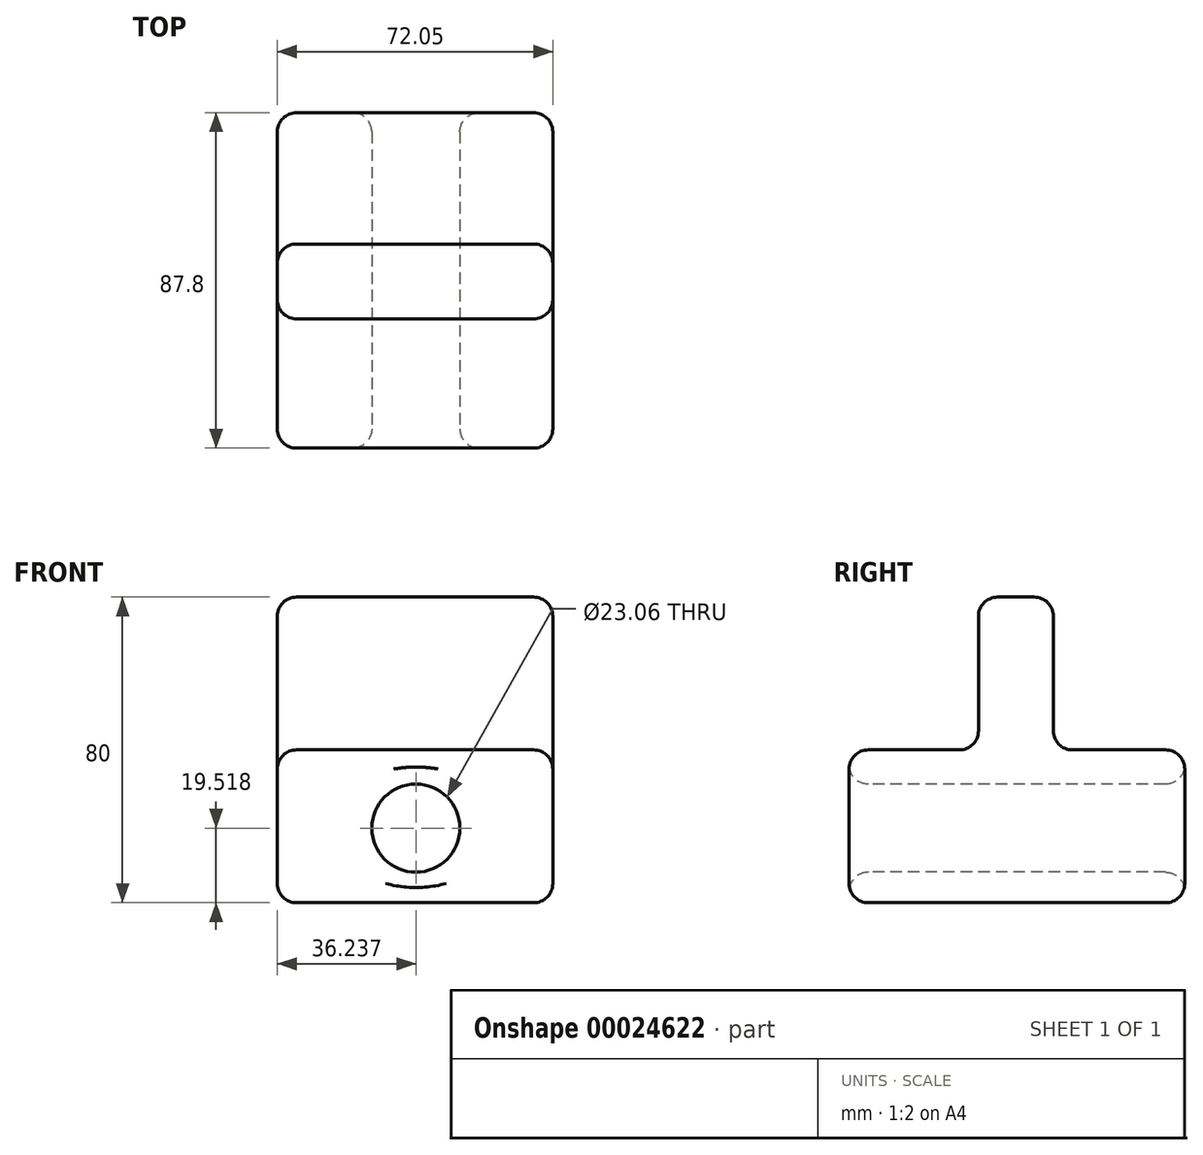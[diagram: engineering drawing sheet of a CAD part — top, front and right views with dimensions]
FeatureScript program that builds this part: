
annotation { "Feature Type Name" : "Feature", "Feature Type Description" : "" }
export const myFeature = defineFeature(function(context is Context, id is Id, definition is map)
    precondition{}
    {
        {
            var Q0;
            Q0=qCreatedBy(makeId("Top.planeOp"),FACE);
            var sketch = newSketch(context, id + "F0", { "sketchPlane" : qUnion([Q0])});
            skLineSegment(sketch, "E0.bottom", {"start": v(-59.89, -44.54) * mm, "end": v(12.16, -44.54) * mm});
            skLineSegment(sketch, "E0.top", {"start": v(-59.89, 43.26) * mm, "end": v(12.16, 43.26) * mm});
            skLineSegment(sketch, "E0.left", {"start": v(-59.89, -44.54) * mm, "end": v(-59.89, 43.26) * mm});
            skLineSegment(sketch, "E0.right", {"start": v(12.16, -44.54) * mm, "end": v(12.16, 43.26) * mm});
            skSolve(sketch);
        }
        {
            var Q0;
            Q0=makeQuery(id+"F0.imprint","IMPRINT",FACE,{"disambiguationData":[TD([[makeQuery(id+"F0.imprint","IMPRINT",EDGE,{"derivedFrom":sQuery(id+"F0.wireOp",EDGE,"E0.bottom")}),1.0]])]});
            extrude(context, id + "F1", {"entities" : qUnion([Q0]), "depth" : 40 * mm});
        }
        {
            var Q0;
            Q0=makeQuery(id+"F1.opExtrude","SWEPT_FACE",FACE,{"disambiguationData":[OSD([sQuery(id+"F0.wireOp",EDGE,"E0.bottom")])]});
            var sketch = newSketch(context, id + "F2", { "sketchPlane" : qUnion([Q0])});
            skCircle(sketch, "E1", {"center": v(-23.65, 19.52) * mm, "radius": 11.53 * mm});
            skSolve(sketch);
        }
        {
            var Q0;
            Q0=makeQuery(id+"F2.imprint","IMPRINT",FACE,{"disambiguationData":[TD([[makeQuery(id+"F2.imprint","IMPRINT",EDGE,{"derivedFrom":sQuery(id+"F2.wireOp",EDGE,"E1")}),1.0]])]});
            extrude(context, id + "F3", {"entities" : qUnion([Q0]), "operationType" : NewBodyOperationType.REMOVE, "endBound" : BoundingType.THROUGH_ALL, "oppositeDirection" : true, "depth" : 25 * mm});
        }
        {
            var Q0;
            Q0=makeQuery(id+"F1.opExtrude","CAP_FACE",FACE,{"disambiguationData":[OSD([sQuery(id+"F0.wireOp",EDGE,"E0.bottom"),sQuery(id+"F0.wireOp",EDGE,"E0.top"),sQuery(id+"F0.wireOp",EDGE,"E0.left"),sQuery(id+"F0.wireOp",EDGE,"E0.right")])],"isStart":false});
            var sketch = newSketch(context, id + "F4", { "sketchPlane" : qUnion([Q0])});
            skLineSegment(sketch, "E2.bottom", {"start": v(-59.89, -10.7) * mm, "end": v(12.16, -10.7) * mm});
            skLineSegment(sketch, "E2.top", {"start": v(-59.89, 8.88) * mm, "end": v(12.16, 8.88) * mm});
            skLineSegment(sketch, "E2.left", {"start": v(-59.89, -10.7) * mm, "end": v(-59.89, 8.88) * mm});
            skLineSegment(sketch, "E2.right", {"start": v(12.16, -10.7) * mm, "end": v(12.16, 8.88) * mm});
            skSolve(sketch);
        }
        {
            var Q0;
            Q0=makeQuery(id+"F4.imprint","IMPRINT",FACE,{"disambiguationData":[TD([[makeQuery(id+"F4.imprint","IMPRINT",EDGE,{"derivedFrom":sQuery(id+"F4.wireOp",EDGE,"E2.bottom")}),1.0]])]});
            extrude(context, id + "F5", {"entities" : qUnion([Q0]), "operationType" : NewBodyOperationType.ADD, "depth" : 40 * mm});
        }
        {
            var Q0;
            Q0=makeQuery(id+"F5.opExtrude","SWEPT_FACE",FACE,{"disambiguationData":[OSD([sQuery(id+"F4.wireOp",EDGE,"E2.bottom")])]});
            var Q1;
            {var subQ0=sQuery(id+"F0.wireOp",EDGE,"E0.bottom");var subQ1=sQuery(id+"F0.wireOp",EDGE,"E0.left");var subQ2=sQuery(id+"F0.wireOp",EDGE,"E0.right");Q1=makeQuery(id+"F5.boolean.opBoolean","SPLIT",FACE,{"disambiguationData":[TD([makeQuery(id+"F1.opExtrude","SWEPT_FACE",FACE,{"disambiguationData":[OSD([subQ0])]})])],"derivedFrom":makeQuery(id+"F1.opExtrude","CAP_FACE",FACE,{"disambiguationData":[OSD([subQ0,sQuery(id+"F0.wireOp",EDGE,"E0.top"),subQ1,subQ2])],"isStart":false})});}
            var Q2;
            Q2=makeQuery(id+"F5.boolean.opBoolean","MERGE",FACE,{"derivedFrom":[makeQuery(id+"F1.opExtrude","SWEPT_FACE",FACE,{"disambiguationData":[OSD([sQuery(id+"F0.wireOp",EDGE,"E0.right")])]}),makeQuery(id+"F5.opExtrude","SWEPT_FACE",FACE,{"disambiguationData":[OSD([sQuery(id+"F4.wireOp",EDGE,"E2.right")])]})]});
            var Q3;
            Q3=makeQuery(id+"F1.opExtrude","SWEPT_FACE",FACE,{"disambiguationData":[OSD([sQuery(id+"F0.wireOp",EDGE,"E0.bottom")])]});
            var Q4;
            Q4=makeQuery(id+"F3.boolean.opBoolean","COPY",FACE,{"derivedFrom":makeQuery(id+"F3.opExtrude","SWEPT_FACE",FACE,{"disambiguationData":[OSD([sQuery(id+"F2.wireOp",EDGE,"E1")])]})});
            var Q5;
            Q5=makeQuery(id+"F5.opExtrude","SWEPT_FACE",FACE,{"disambiguationData":[OSD([sQuery(id+"F4.wireOp",EDGE,"E2.top")])]});
            var Q6;
            Q6=makeQuery(id+"F1.opExtrude","SWEPT_FACE",FACE,{"disambiguationData":[OSD([sQuery(id+"F0.wireOp",EDGE,"E0.top")])]});
            var Q7;
            Q7=makeQuery(id+"F1.opExtrude","CAP_FACE",FACE,{"disambiguationData":[OSD([sQuery(id+"F0.wireOp",EDGE,"E0.bottom"),sQuery(id+"F0.wireOp",EDGE,"E0.top"),sQuery(id+"F0.wireOp",EDGE,"E0.left"),sQuery(id+"F0.wireOp",EDGE,"E0.right")])],"isStart":true});
            var Q8;
            Q8=makeQuery(id+"F5.boolean.opBoolean","MERGE",FACE,{"derivedFrom":[makeQuery(id+"F1.opExtrude","SWEPT_FACE",FACE,{"disambiguationData":[OSD([sQuery(id+"F0.wireOp",EDGE,"E0.left")])]}),makeQuery(id+"F5.opExtrude","SWEPT_FACE",FACE,{"disambiguationData":[OSD([sQuery(id+"F4.wireOp",EDGE,"E2.left")])]})]});
            fillet(context, id + "F6", {"entities" : qUnion([Q0, Q1, Q2, Q3, Q4, Q5, Q6, Q7, Q8]), "radius" : 5 * mm, "tangentPropagation" : true, "allowEdgeOverflow" : false});
        }
    });
